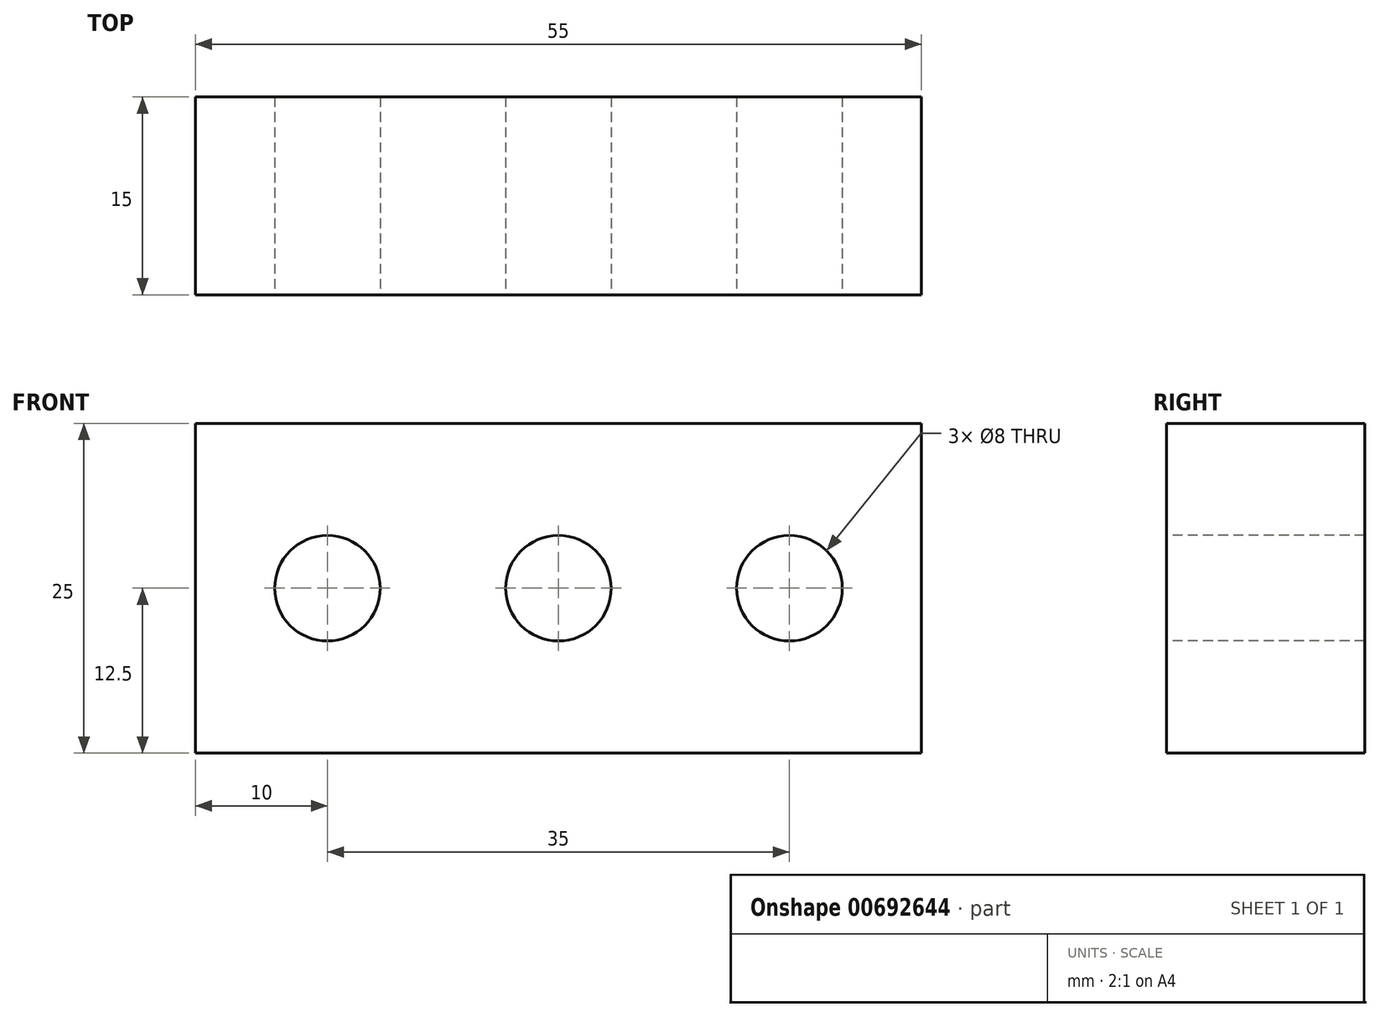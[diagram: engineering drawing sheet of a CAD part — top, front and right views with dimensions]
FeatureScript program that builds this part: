
annotation { "Feature Type Name" : "Feature", "Feature Type Description" : "" }
export const myFeature = defineFeature(function(context is Context, id is Id, definition is map)
    precondition{}
    {
        {
            var Q0;
            Q0=qCreatedBy(makeId("Top.planeOp"),FACE);
            var sketch = newSketch(context, id + "F0", { "sketchPlane" : qUnion([Q0])});
            skLineSegment(sketch, "E0.bottom", {"start": v(0, 26.12) * mm, "end": v(-55, 26.12) * mm});
            skLineSegment(sketch, "E0.top", {"start": v(0, 41.12) * mm, "end": v(-55, 41.12) * mm});
            skLineSegment(sketch, "E0.left", {"start": v(0, 26.12) * mm, "end": v(0, 41.12) * mm});
            skLineSegment(sketch, "E0.right", {"start": v(-55, 26.12) * mm, "end": v(-55, 41.12) * mm});
            skPoint(sketch, "E0.middle", {"position": v(-27.5, 33.62) * mm});
            skSolve(sketch);
        }
        {
            var Q0;
            Q0 = qSketchRegion(id + "F0", true);
            extrude(context, id + "F1", {"entities" : qUnion([Q0]), "depth" : 25 * mm, "offsetDistance" : 25 * mm});
        }
        {
            var Q0;
            Q0=makeQuery(id+"F1.opExtrude","SWEPT_FACE",FACE,{"disambiguationData":[OSD([sQuery(id+"F0.wireOp",EDGE,"E0.bottom")])]});
            var sketch = newSketch(context, id + "F2", { "sketchPlane" : qUnion([Q0])});
            skCircle(sketch, "E1", {"center": v(-27.5, 12.5) * mm, "radius": 4 * mm});
            skPoint(sketch, "E1.centerSnap0", {"position": v(0, 12.5) * mm});
            skPoint(sketch, "E1.centerSnap1", {"position": v(-27.5, 25) * mm});
            skCircle(sketch, "E2", {"center": v(-10, 12.5) * mm, "radius": 4 * mm});
            skCircle(sketch, "E3", {"center": v(-45, 12.5) * mm, "radius": 4 * mm});
            skPoint(sketch, "E3.centerSnap0", {"position": v(-55, 12.5) * mm});
            skSolve(sketch);
        }
        {
            var Q0;
            Q0=makeQuery(id+"F2.imprint","IMPRINT",FACE,{"disambiguationData":[TD([[makeQuery(id+"F2.imprint","IMPRINT",EDGE,{"derivedFrom":sQuery(id+"F2.wireOp",EDGE,"E2")}),1.0]])]});
            var Q1;
            Q1=makeQuery(id+"F2.imprint","IMPRINT",FACE,{"disambiguationData":[TD([[makeQuery(id+"F2.imprint","IMPRINT",EDGE,{"derivedFrom":sQuery(id+"F2.wireOp",EDGE,"E3")}),1.0]])]});
            var Q2;
            Q2=makeQuery(id+"F2.imprint","IMPRINT",FACE,{"disambiguationData":[TD([[makeQuery(id+"F2.imprint","IMPRINT",EDGE,{"derivedFrom":sQuery(id+"F2.wireOp",EDGE,"E1")}),1.0]])]});
            extrude(context, id + "F3", {"entities" : qUnion([Q0, Q1, Q2]), "operationType" : NewBodyOperationType.REMOVE, "oppositeDirection" : true, "depth" : 25 * mm, "offsetDistance" : 25 * mm});
        }
    });
